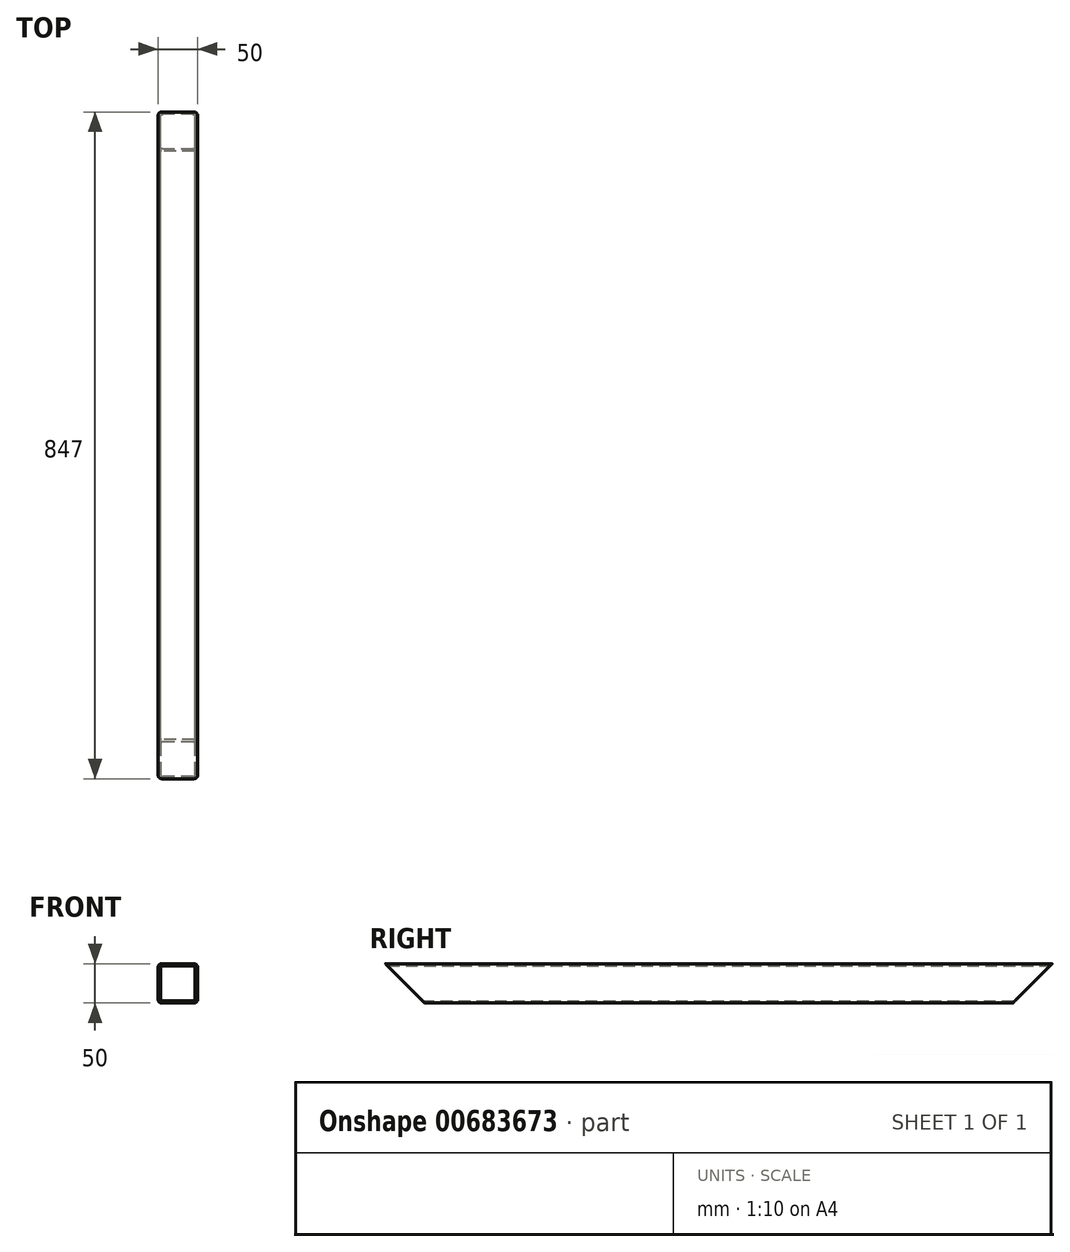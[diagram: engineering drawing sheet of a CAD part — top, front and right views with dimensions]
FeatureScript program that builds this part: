
annotation { "Feature Type Name" : "Feature", "Feature Type Description" : "" }
export const myFeature = defineFeature(function(context is Context, id is Id, definition is map)
    precondition{}
    {
        {
            var Q0;
            Q0=qCreatedBy(makeId("Front.planeOp"),FACE);
            var sketch = newSketch(context, id + "F0", { "sketchPlane" : qUnion([Q0])});
            skLineSegment(sketch, "E0.bottom", {"start": v(4.5, 0) * mm, "end": v(45.5, 0) * mm});
            skLineSegment(sketch, "E0.top", {"start": v(4.5, -50) * mm, "end": v(45.5, -50) * mm});
            skLineSegment(sketch, "E0.left", {"start": v(0, -4.5) * mm, "end": v(0, -45.5) * mm});
            skLineSegment(sketch, "E0.right", {"start": v(50, -4.5) * mm, "end": v(50, -45.5) * mm});
            skLineSegment(sketch, "E1.0", {"start": v(6, -3) * mm, "end": v(44, -3) * mm});
            skLineSegment(sketch, "E1.1", {"start": v(3, -6) * mm, "end": v(3, -44) * mm});
            skLineSegment(sketch, "E1.2", {"start": v(6, -47) * mm, "end": v(44, -47) * mm});
            skLineSegment(sketch, "E1.3", {"start": v(47, -6) * mm, "end": v(47, -44) * mm});
            skPoint(sketch, "E2.visualSharp", {"position": v(3, -3) * mm});
            skArc(sketch, "E2.filletArc", {"start": v(6, -3) * mm, "mid": v(3.88, -3.88) * mm, "end": v(3, -6) * mm});
            skPoint(sketch, "E3.visualSharp", {"position": v(47, -3) * mm});
            skArc(sketch, "E3.filletArc", {"start": v(47, -6) * mm, "mid": v(46.12, -3.88) * mm, "end": v(44, -3) * mm});
            skPoint(sketch, "E4.visualSharp", {"position": v(3, -47) * mm});
            skArc(sketch, "E4.filletArc", {"start": v(3, -44) * mm, "mid": v(3.88, -46.12) * mm, "end": v(6, -47) * mm});
            skPoint(sketch, "E5.visualSharp", {"position": v(47, -47) * mm});
            skArc(sketch, "E5.filletArc", {"start": v(44, -47) * mm, "mid": v(46.12, -46.12) * mm, "end": v(47, -44) * mm});
            skPoint(sketch, "E6.visualSharp", {"position": v(0, 0) * mm});
            skArc(sketch, "E6.filletArc", {"start": v(4.5, 0) * mm, "mid": v(1.32, -1.32) * mm, "end": v(0, -4.5) * mm});
            skPoint(sketch, "E7.visualSharp", {"position": v(50, 0) * mm});
            skArc(sketch, "E7.filletArc", {"start": v(50, -4.5) * mm, "mid": v(48.68, -1.32) * mm, "end": v(45.5, 0) * mm});
            skPoint(sketch, "E8.visualSharp", {"position": v(50, -50) * mm});
            skArc(sketch, "E8.filletArc", {"start": v(45.5, -50) * mm, "mid": v(48.68, -48.68) * mm, "end": v(50, -45.5) * mm});
            skPoint(sketch, "E9.visualSharp", {"position": v(0, -50) * mm});
            skArc(sketch, "E9.filletArc", {"start": v(0, -45.5) * mm, "mid": v(1.32, -48.68) * mm, "end": v(4.5, -50) * mm});
            skSolve(sketch);
        }
        {
            var Q0;
            Q0=makeQuery(id+"F0.imprint","IMPRINT",FACE,{"disambiguationData":[TD([[makeQuery(id+"F0.imprint","IMPRINT",EDGE,{"derivedFrom":sQuery(id+"F0.wireOp",EDGE,"E0.bottom")}),-1.0]])]});
            extrude(context, id + "F1", {"entities" : qUnion([Q0]), "depth" : 847 * mm, "offsetDistance" : 25 * mm});
        }
        {
            var Q0;
            Q0=qCreatedBy(makeId("Right.planeOp"),FACE);
            var sketch = newSketch(context, id + "F2", { "sketchPlane" : qUnion([Q0])});
            skLineSegment(sketch, "E10.0", {"start": v(0, -4.5) * mm, "end": v(0, -45.5) * mm});
            skLineSegment(sketch, "E11", {"start": v(0, 0) * mm, "end": v(-70.71, -70.71) * mm});
            skLineSegment(sketch, "E12", {"start": v(-70.71, -70.71) * mm, "end": v(29.29, -70.71) * mm});
            skLineSegment(sketch, "E13", {"start": v(29.29, -70.71) * mm, "end": v(29.29, 0) * mm});
            skLineSegment(sketch, "E14", {"start": v(29.29, 0) * mm, "end": v(0, 0) * mm});
            skLineSegment(sketch, "E15.0", {"start": v(-847, -45.5) * mm, "end": v(0, -45.5) * mm});
            skLineSegment(sketch, "E16", {"start": v(-423.5, -45.5) * mm, "end": v(-423.5, 29.62) * mm, "construction": true});
            skLineSegment(sketch, "E17.MirrorCS", {"start": v(-876.29, -70.71) * mm, "end": v(-876.29, 0) * mm});
            skLineSegment(sketch, "E18.MirrorCS", {"start": v(-876.29, 0) * mm, "end": v(-847, 0) * mm});
            skLineSegment(sketch, "E19.MirrorCS", {"start": v(-847, 0) * mm, "end": v(-776.29, -70.71) * mm});
            skLineSegment(sketch, "E20.MirrorCS", {"start": v(-776.29, -70.71) * mm, "end": v(-876.29, -70.71) * mm});
            skSolve(sketch);
        }
        {
            var Q0;
            Q0=makeQuery(id+"F2.imprint","IMPRINT",FACE,{"disambiguationData":[TD([[makeQuery(id+"F2.imprint","IMPRINT",EDGE,{"derivedFrom":sQuery(id+"F2.wireOp",EDGE,"E11")}),1.0]])]});
            var Q1;
            Q1=makeQuery(id+"F2.imprint","IMPRINT",FACE,{"disambiguationData":[TD([[makeQuery(id+"F2.imprint","IMPRINT",EDGE,{"derivedFrom":sQuery(id+"F2.wireOp",EDGE,"E17.MirrorCS")}),-1.0]])]});
            extrude(context, id + "F3", {"entities" : qUnion([Q0, Q1]), "operationType" : NewBodyOperationType.REMOVE, "endBound" : BoundingType.THROUGH_ALL, "depth" : 25 * mm, "offsetDistance" : 25 * mm});
        }
    });
